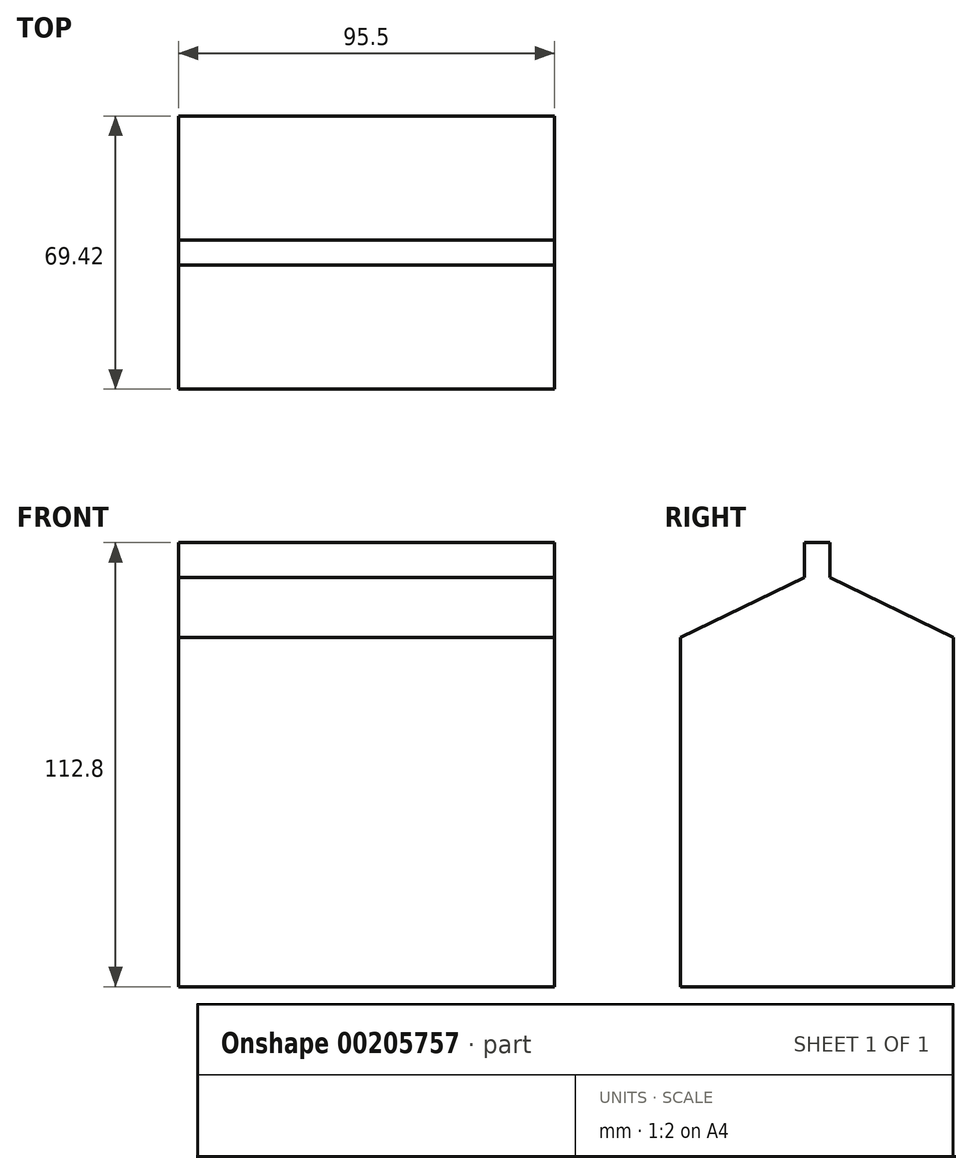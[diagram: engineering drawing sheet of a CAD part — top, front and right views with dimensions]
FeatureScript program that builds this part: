
annotation { "Feature Type Name" : "Feature", "Feature Type Description" : "" }
export const myFeature = defineFeature(function(context is Context, id is Id, definition is map)
    precondition{}
    {
        {
            var Q0;
            Q0=qCreatedBy(makeId("Right.planeOp"),FACE);
            var sketch = newSketch(context, id + "F0", { "sketchPlane" : qUnion([Q0])});
            skLineSegment(sketch, "E0.bottom", {"start": v(34.7, -46.31) * mm, "end": v(-34.7, -46.31) * mm});
            skLineSegment(sketch, "E0.left", {"start": v(34.7, -46.31) * mm, "end": v(34.7, 42.48) * mm});
            skLineSegment(sketch, "E0.right", {"start": v(-34.7, -46.31) * mm, "end": v(-34.7, 42.48) * mm});
            skPoint(sketch, "E0.middle", {"position": v(0, -1.92) * mm});
            skLineSegment(sketch, "E1", {"start": v(-34.7, 42.48) * mm, "end": v(-3.23, 57.61) * mm});
            skLineSegment(sketch, "E2", {"start": v(-3.23, 57.61) * mm, "end": v(-3.23, 66.5) * mm});
            skLineSegment(sketch, "E3", {"start": v(-3.23, 66.5) * mm, "end": v(0, 66.5) * mm});
            skLineSegment(sketch, "E4.MirrorCS", {"start": v(34.7, 179.3) * mm, "end": v(-34.7, 179.3) * mm});
            skLineSegment(sketch, "E5.MirrorCS", {"start": v(3.23, 66.5) * mm, "end": v(0, 66.5) * mm});
            skLineSegment(sketch, "E6.MirrorCS", {"start": v(3.23, 57.61) * mm, "end": v(3.23, 66.5) * mm});
            skLineSegment(sketch, "E7.MirrorCS", {"start": v(34.7, 42.48) * mm, "end": v(3.23, 57.61) * mm});
            skSolve(sketch);
        }
        {
            var Q0;
            Q0=makeQuery(id+"F0.imprint","IMPRINT",FACE,{"disambiguationData":[TD([[makeQuery(id+"F0.imprint","IMPRINT",EDGE,{"derivedFrom":sQuery(id+"F0.wireOp",EDGE,"E0.bottom")}),-1.0]])]});
            extrude(context, id + "F1", {"entities" : qUnion([Q0]), "endBound" : BoundingType.SYMMETRIC, "depth" : 95.5 * mm});
        }
    });
